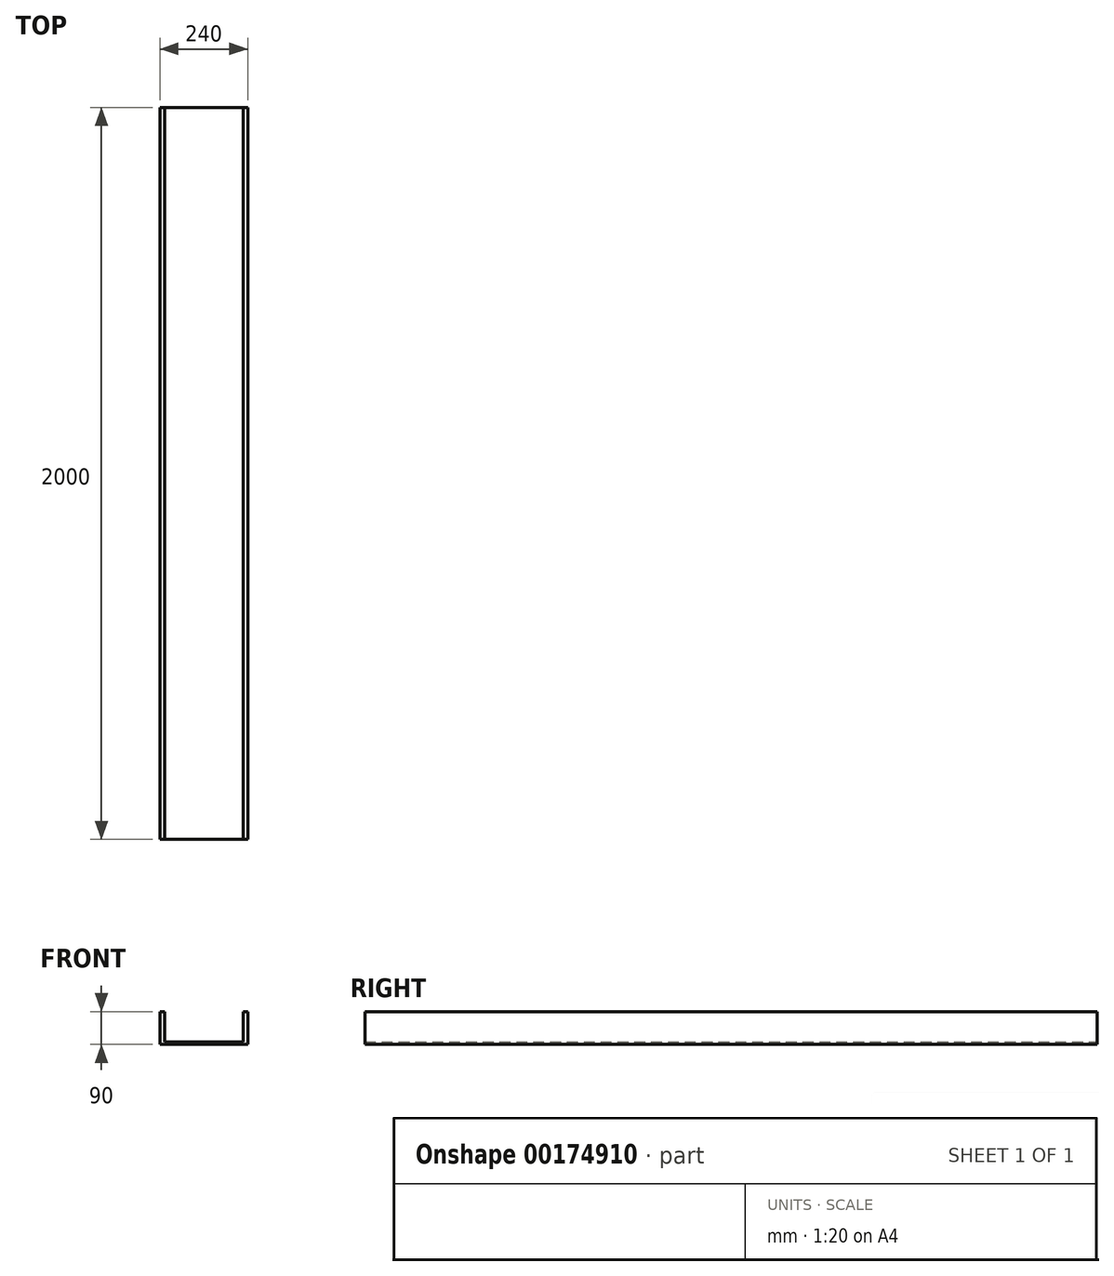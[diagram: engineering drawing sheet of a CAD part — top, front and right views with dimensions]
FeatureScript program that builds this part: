
annotation { "Feature Type Name" : "Feature", "Feature Type Description" : "" }
export const myFeature = defineFeature(function(context is Context, id is Id, definition is map)
    precondition{}
    {
        {
            var Q0;
            Q0=qCreatedBy(makeId("Front.planeOp"),FACE);
            var sketch = newSketch(context, id + "F0", { "sketchPlane" : qUnion([Q0])});
            skLineSegment(sketch, "E0", {"start": v(0, 0) * mm, "end": v(240, 0) * mm});
            skLineSegment(sketch, "E1", {"start": v(240, 0) * mm, "end": v(240, 90) * mm});
            skLineSegment(sketch, "E2", {"start": v(240, 90) * mm, "end": v(227.5, 90) * mm});
            skLineSegment(sketch, "E3", {"start": v(227.5, 90) * mm, "end": v(227.5, 7) * mm});
            skLineSegment(sketch, "E4", {"start": v(227.5, 7) * mm, "end": v(12.5, 7) * mm});
            skLineSegment(sketch, "E5", {"start": v(12.5, 7) * mm, "end": v(12.5, 90) * mm});
            skLineSegment(sketch, "E6", {"start": v(12.5, 90) * mm, "end": v(0, 90) * mm});
            skLineSegment(sketch, "E7", {"start": v(0, 90) * mm, "end": v(0, 0) * mm});
            skSolve(sketch);
        }
        {
            var Q0;
            Q0=qSketchRegion(id+"F0",true);
            extrude(context, id + "F1", {"entities" : qUnion([Q0]), "depth" : 2000 * mm});
        }
    });
